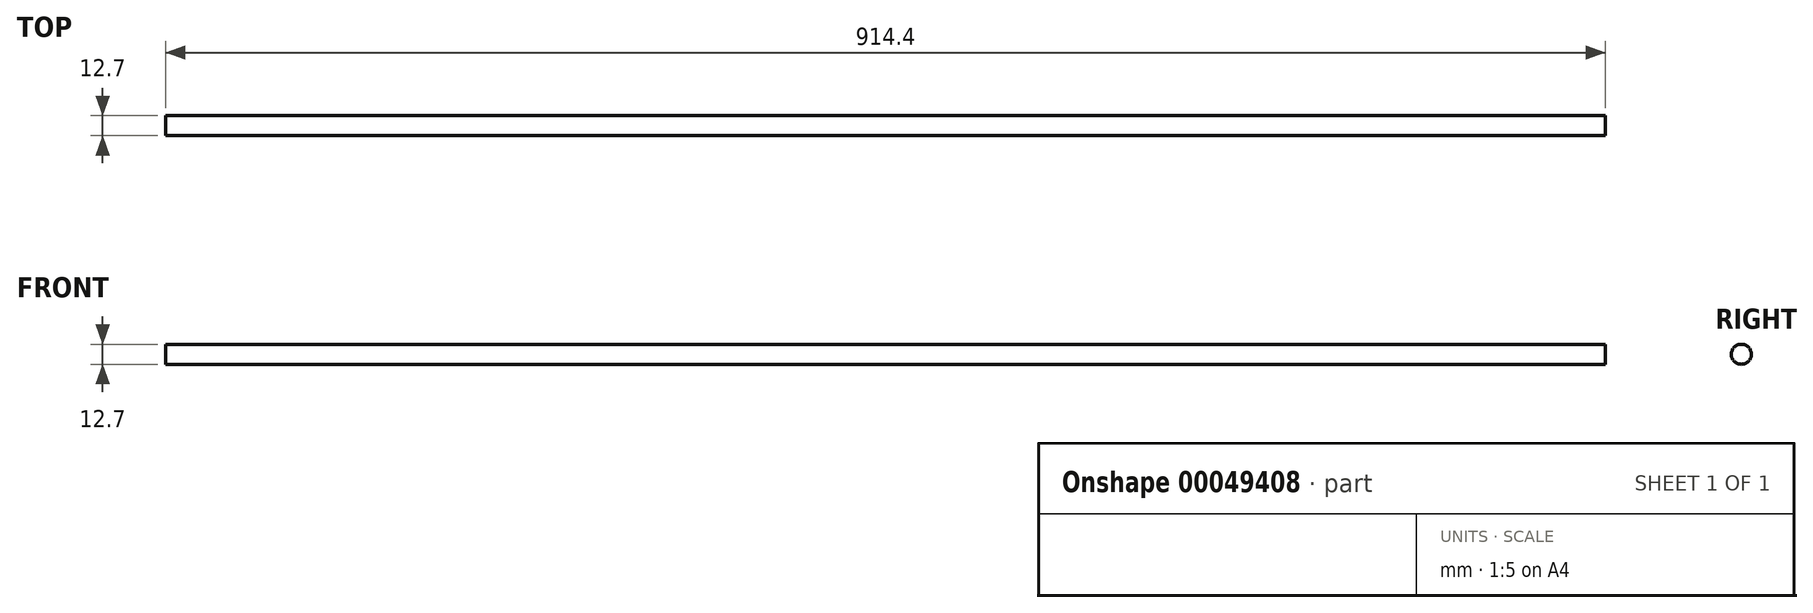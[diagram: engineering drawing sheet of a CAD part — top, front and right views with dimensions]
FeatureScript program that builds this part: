
annotation { "Feature Type Name" : "Feature", "Feature Type Description" : "" }
export const myFeature = defineFeature(function(context is Context, id is Id, definition is map)
    precondition{}
    {
        {
            var Q0;
            Q0=qCreatedBy(makeId("Top.planeOp"),FACE);
            var sketch = newSketch(context, id + "F0", { "sketchPlane" : qUnion([Q0])});
            skLineSegment(sketch, "E0.bottom", {"start": v(0, 0) * mm, "end": v(-914.4, 0) * mm});
            skLineSegment(sketch, "E0.top", {"start": v(0, -25.4) * mm, "end": v(-914.4, -25.4) * mm});
            skLineSegment(sketch, "E0.left", {"start": v(0, 0) * mm, "end": v(0, -25.4) * mm});
            skLineSegment(sketch, "E0.right", {"start": v(-914.4, 0) * mm, "end": v(-914.4, -25.4) * mm});
            skSolve(sketch);
        }
        {
            var Q0;
            Q0=qCreatedBy(makeId("Right.planeOp"),FACE);
            var sketch = newSketch(context, id + "F1", { "sketchPlane" : qUnion([Q0])});
            skCircle(sketch, "E1", {"center": v(0, 0) * mm, "radius": 6.35 * mm});
            skSolve(sketch);
        }
        {
            var Q0;
            Q0 = qSketchRegion(id + "F1", true);
            extrude(context, id + "F2", {"entities" : qUnion([Q0]), "depth" : 914.4 * mm});
        }
    });
